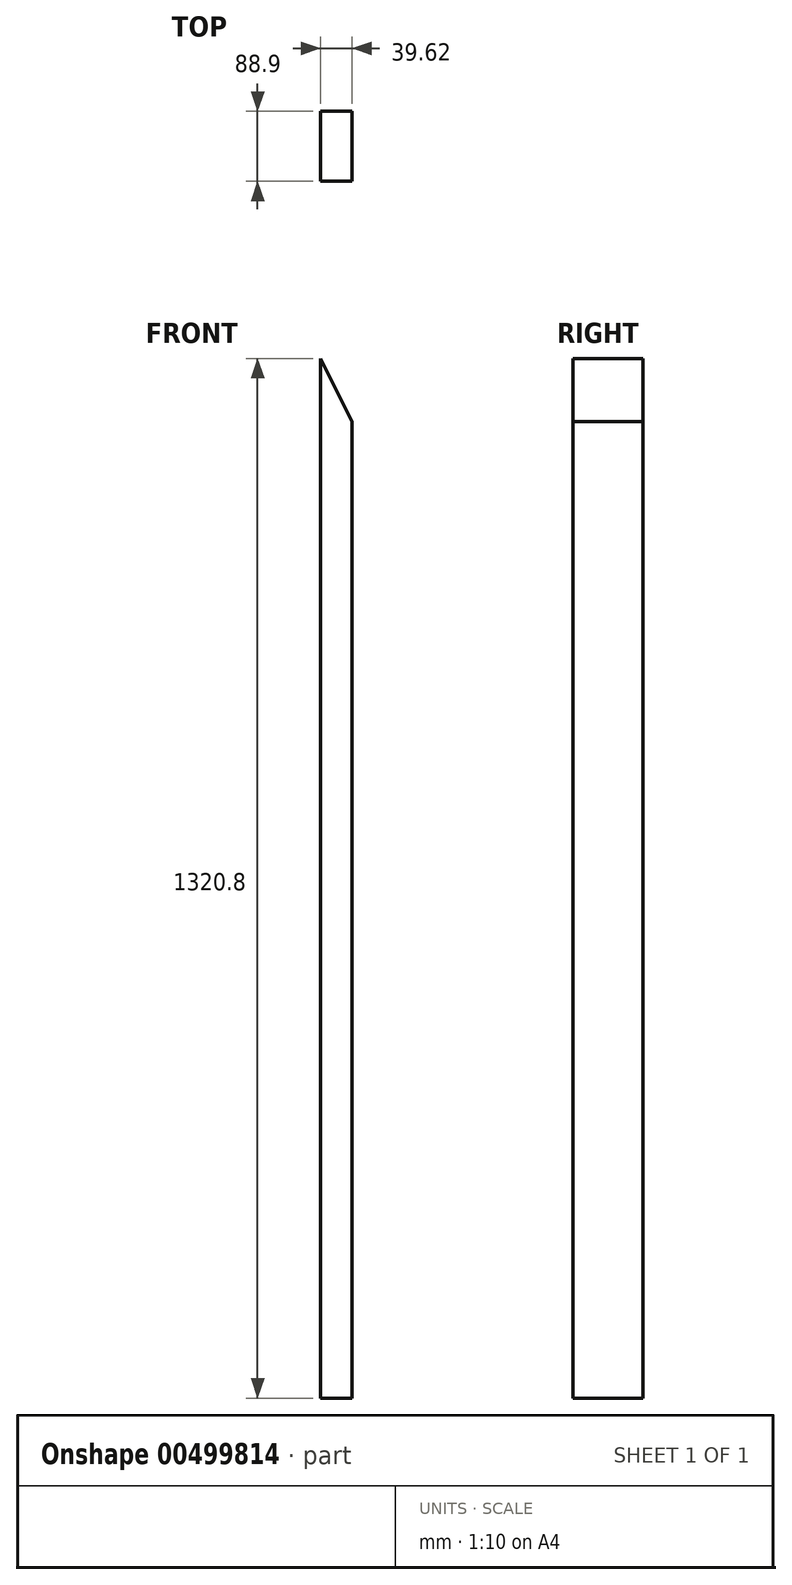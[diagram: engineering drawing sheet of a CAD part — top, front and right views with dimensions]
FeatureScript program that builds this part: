
annotation { "Feature Type Name" : "Feature", "Feature Type Description" : "" }
export const myFeature = defineFeature(function(context is Context, id is Id, definition is map)
    precondition{}
    {
        {
            var Q0;
            Q0=qCreatedBy(makeId("Front.planeOp"),FACE);
            var sketch = newSketch(context, id + "F0", { "sketchPlane" : qUnion([Q0])});
            skLineSegment(sketch, "E0.top", {"start": v(19.81, -660.4) * mm, "end": v(-19.81, -660.4) * mm});
            skLineSegment(sketch, "E0.left", {"start": v(19.81, 580.05) * mm, "end": v(19.81, -660.4) * mm});
            skLineSegment(sketch, "E0.right", {"start": v(-19.81, 660.4) * mm, "end": v(-19.81, -660.4) * mm});
            skPoint(sketch, "E0.middle", {"position": v(0, 0) * mm});
            skLineSegment(sketch, "E1", {"start": v(-19.81, 660.4) * mm, "end": v(19.81, 580.05) * mm});
            skSolve(sketch);
        }
        {
            var Q0;
            Q0 = qSketchRegion(id + "F0", true);
            extrude(context, id + "F1", {"entities" : qUnion([Q0]), "depth" : 88.9 * mm});
        }
    });
